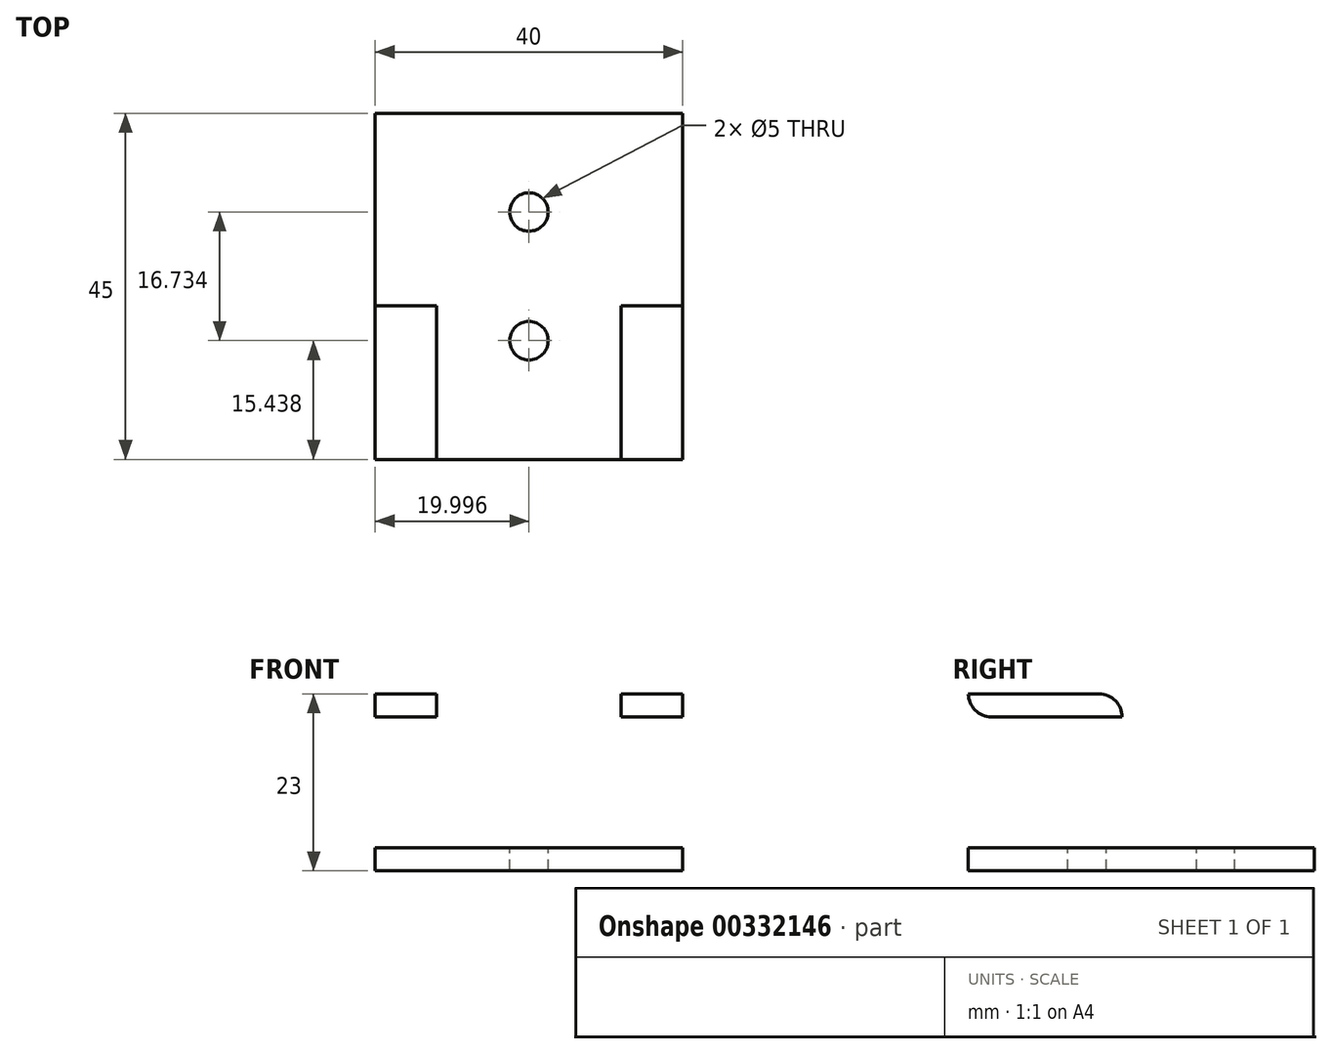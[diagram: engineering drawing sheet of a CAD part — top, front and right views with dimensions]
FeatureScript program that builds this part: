
annotation { "Feature Type Name" : "Feature", "Feature Type Description" : "" }
export const myFeature = defineFeature(function(context is Context, id is Id, definition is map)
    precondition{}
    {
        {
            var Q0;
            Q0=qCreatedBy(makeId("Top.planeOp"),FACE);
            var sketch = newSketch(context, id + "F0", { "sketchPlane" : qUnion([Q0])});
            skLineSegment(sketch, "E0.bottom", {"start": v(-45.6, 18.98) * mm, "end": v(-5.6, 18.98) * mm});
            skLineSegment(sketch, "E0.top", {"start": v(-45.6, -31.02) * mm, "end": v(-5.6, -31.02) * mm});
            skLineSegment(sketch, "E0.left", {"start": v(-45.6, 18.98) * mm, "end": v(-45.6, -31.02) * mm});
            skLineSegment(sketch, "E0.right", {"start": v(-5.6, 18.98) * mm, "end": v(-5.6, -31.02) * mm});
            skLineSegment(sketch, "E1.top", {"start": v(-45.6, -26.02) * mm, "end": v(-5.6, -26.02) * mm});
            skLineSegment(sketch, "E1.left", {"start": v(-45.6, -31.02) * mm, "end": v(-45.6, -26.02) * mm});
            skLineSegment(sketch, "E1.right", {"start": v(-5.6, -31.02) * mm, "end": v(-5.6, -26.02) * mm});
            skPoint(sketch, "E2.oppositeSnap0", {"position": v(-45.6, -6.02) * mm});
            skLineSegment(sketch, "E2.bottom", {"start": v(-45.6, -31.02) * mm, "end": v(-37.6, -31.02) * mm});
            skLineSegment(sketch, "E2.top", {"start": v(-45.6, -6.02) * mm, "end": v(-37.6, -6.02) * mm});
            skLineSegment(sketch, "E2.left", {"start": v(-45.6, -31.02) * mm, "end": v(-45.6, -6.02) * mm});
            skLineSegment(sketch, "E2.right", {"start": v(-37.6, -31.02) * mm, "end": v(-37.6, -6.02) * mm});
            skLineSegment(sketch, "E3.bottom", {"start": v(-5.6, -31.02) * mm, "end": v(-13.6, -31.02) * mm});
            skLineSegment(sketch, "E3.top", {"start": v(-5.6, -6.02) * mm, "end": v(-13.6, -6.02) * mm});
            skLineSegment(sketch, "E3.left", {"start": v(-5.6, -31.02) * mm, "end": v(-5.6, -6.02) * mm});
            skLineSegment(sketch, "E3.right", {"start": v(-13.6, -31.02) * mm, "end": v(-13.6, -6.02) * mm});
            skCircle(sketch, "E4", {"center": v(-25.6, 6.15) * mm, "radius": 2.5 * mm});
            skCircle(sketch, "E5", {"center": v(-25.6, -10.58) * mm, "radius": 2.5 * mm});
            skPoint(sketch, "E6", {"position": v(-25.6, 18.98) * mm});
            skSolve(sketch);
        }
        {
            var Q0;
            Q0=makeQuery(id+"F0.imprint","IMPRINT",FACE,{"disambiguationData":[TD([[makeQuery(id+"F0.imprint","IMPRINT",EDGE,{"derivedFrom":sQuery(id+"F0.wireOp",EDGE,"E0.bottom")}),-1.0]])]});
            var Q1;
            {var subQ5=sQuery(id+"F0.wireOp",EDGE,"E2.top");Q1=makeQuery(id+"F0.imprint","IMPRINT",FACE,{"disambiguationData":[TD([[makeQuery(id+"F0.imprint","IMPRINT",EDGE,{"derivedFrom":subQ5}),-1.0]])]});}
            var Q2;
            {var subQ5=sQuery(id+"F0.wireOp",EDGE,"E2.bottom");Q2=makeQuery(id+"F0.imprint","IMPRINT",FACE,{"disambiguationData":[TD([[makeQuery(id+"F0.imprint","IMPRINT",EDGE,{"derivedFrom":subQ5}),1.0]])]});}
            var Q3;
            {var subQ0=sQuery(id+"F0.wireOp",EDGE,"E0.top");Q3=makeQuery(id+"F0.imprint","IMPRINT",FACE,{"disambiguationData":[TD([[makeQuery(id+"F0.imprint","IMPRINT",EDGE,{"derivedFrom":subQ0}),1.0]])]});}
            var Q4;
            {var subQ5=sQuery(id+"F0.wireOp",EDGE,"E3.bottom");Q4=makeQuery(id+"F0.imprint","IMPRINT",FACE,{"disambiguationData":[TD([[makeQuery(id+"F0.imprint","IMPRINT",EDGE,{"derivedFrom":subQ5}),-1.0]])]});}
            var Q5;
            {var subQ5=sQuery(id+"F0.wireOp",EDGE,"E3.top");Q5=makeQuery(id+"F0.imprint","IMPRINT",FACE,{"disambiguationData":[TD([[makeQuery(id+"F0.imprint","IMPRINT",EDGE,{"derivedFrom":subQ5}),1.0]])]});}
            extrude(context, id + "F1", {"entities" : qUnion([Q0, Q1, Q2, Q3, Q4, Q5]), "oppositeDirection" : true, "depth" : 3 * mm});
        }
        {
            var Q0;
            {var subQ5=sQuery(id+"F0.wireOp",EDGE,"E2.top");Q0=makeQuery(id+"F0.imprint","IMPRINT",FACE,{"disambiguationData":[TD([[makeQuery(id+"F0.imprint","IMPRINT",EDGE,{"derivedFrom":subQ5}),-1.0]])]});}
            var Q1;
            {var subQ5=sQuery(id+"F0.wireOp",EDGE,"E3.top");Q1=makeQuery(id+"F0.imprint","IMPRINT",FACE,{"disambiguationData":[TD([[makeQuery(id+"F0.imprint","IMPRINT",EDGE,{"derivedFrom":subQ5}),1.0]])]});}
            var Q2;
            {var subQ5=sQuery(id+"F0.wireOp",EDGE,"E3.bottom");Q2=makeQuery(id+"F0.imprint","IMPRINT",FACE,{"disambiguationData":[TD([[makeQuery(id+"F0.imprint","IMPRINT",EDGE,{"derivedFrom":subQ5}),-1.0]])]});}
            var Q3;
            {var subQ5=sQuery(id+"F0.wireOp",EDGE,"E2.bottom");Q3=makeQuery(id+"F0.imprint","IMPRINT",FACE,{"disambiguationData":[TD([[makeQuery(id+"F0.imprint","IMPRINT",EDGE,{"derivedFrom":subQ5}),1.0]])]});}
            extrude(context, id + "F2", {"entities" : qUnion([Q0, Q1, Q2, Q3]), "operationType" : NewBodyOperationType.ADD, "depth" : 20 * mm});
        }
        {
            var Q0;
            {var subQ5=sQuery(id+"F0.wireOp",EDGE,"E2.top");Q0=makeQuery(id+"F0.imprint","IMPRINT",FACE,{"disambiguationData":[TD([[makeQuery(id+"F0.imprint","IMPRINT",EDGE,{"derivedFrom":subQ5}),-1.0]])]});}
            var Q1;
            {var subQ5=sQuery(id+"F0.wireOp",EDGE,"E3.top");Q1=makeQuery(id+"F0.imprint","IMPRINT",FACE,{"disambiguationData":[TD([[makeQuery(id+"F0.imprint","IMPRINT",EDGE,{"derivedFrom":subQ5}),1.0]])]});}
            extrude(context, id + "F3", {"entities" : qUnion([Q0, Q1]), "operationType" : NewBodyOperationType.REMOVE, "depth" : 17 * mm});
        }
        {
            var Q0;
            Q0=makeQuery(id+"F2.opExtrude","CAP_EDGE",EDGE,{"disambiguationData":[OSD([sQuery(id+"F0.wireOp",EDGE,"E2.bottom")])],"isStart":false});
            var Q1;
            Q1=makeQuery(id+"F2.opExtrude","CAP_EDGE",EDGE,{"disambiguationData":[OSD([sQuery(id+"F0.wireOp",EDGE,"E3.bottom")])],"isStart":false});
            var Q2;
            Q2=makeQuery(id+"F2.opExtrude","CAP_EDGE",EDGE,{"disambiguationData":[OSD([sQuery(id+"F0.wireOp",EDGE,"E2.top")])],"isStart":false});
            var Q3;
            Q3=makeQuery(id+"F2.opExtrude","CAP_EDGE",EDGE,{"disambiguationData":[OSD([sQuery(id+"F0.wireOp",EDGE,"E3.top")])],"isStart":false});
            var Q4;
            {var subQ0=sQuery(id+"F0.wireOp",EDGE,"E1.top");Q4=makeQuery(id+"F3.boolean.opBoolean","COPY",EDGE,{"derivedFrom":makeQuery(id+"F3.opExtrude","CAP_EDGE",EDGE,{"disambiguationData":[OSD([subQ0]),TDD([makeQuery(id+"F0.imprint","IMPRINT",EDGE,{"disambiguationData":[TD([[makeQuery(id+"F0.imprint","INTERSECT",VERTEX,{"derivedFrom":[subQ0,sQuery(id+"F0.wireOp",EDGE,"E2.left")]}),-1.0]])],"derivedFrom":subQ0})])],"isStart":false})});}
            var Q5;
            {var subQ0=sQuery(id+"F0.wireOp",EDGE,"E1.top");Q5=makeQuery(id+"F3.boolean.opBoolean","COPY",EDGE,{"derivedFrom":makeQuery(id+"F3.opExtrude","CAP_EDGE",EDGE,{"disambiguationData":[OSD([subQ0]),TDD([makeQuery(id+"F0.imprint","IMPRINT",EDGE,{"disambiguationData":[TD([[makeQuery(id+"F0.imprint","INTERSECT",VERTEX,{"derivedFrom":[subQ0,sQuery(id+"F0.wireOp",EDGE,"E3.left")]}),1.0]])],"derivedFrom":subQ0})])],"isStart":false})});}
            var Q6;
            {var subQ0=sQuery(id+"F0.wireOp",EDGE,"E1.top");Q6=makeQuery(id+"F3.boolean.opBoolean","COPY",EDGE,{"derivedFrom":makeQuery(id+"F3.opExtrude","CAP_EDGE",EDGE,{"disambiguationData":[OSD([subQ0]),TDD([makeQuery(id+"F0.imprint","IMPRINT",EDGE,{"disambiguationData":[TD([[makeQuery(id+"F0.imprint","INTERSECT",VERTEX,{"derivedFrom":[subQ0,sQuery(id+"F0.wireOp",EDGE,"E3.left")]}),1.0]])],"derivedFrom":subQ0})])],"isStart":true})});}
            var Q7;
            {var subQ0=sQuery(id+"F0.wireOp",EDGE,"E1.top");Q7=makeQuery(id+"F3.boolean.opBoolean","COPY",EDGE,{"derivedFrom":makeQuery(id+"F3.opExtrude","CAP_EDGE",EDGE,{"disambiguationData":[OSD([subQ0]),TDD([makeQuery(id+"F0.imprint","IMPRINT",EDGE,{"disambiguationData":[TD([[makeQuery(id+"F0.imprint","INTERSECT",VERTEX,{"derivedFrom":[subQ0,sQuery(id+"F0.wireOp",EDGE,"E2.left")]}),-1.0]])],"derivedFrom":subQ0})])],"isStart":true})});}
            fillet(context, id + "F4", {"entities" : qUnion([Q0, Q1, Q2, Q3, Q4, Q5, Q6, Q7]), "radius" : 3 * mm, "tangentPropagation" : true, "allowEdgeOverflow" : false});
        }
    });
